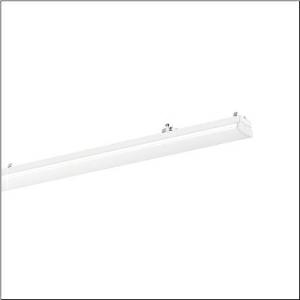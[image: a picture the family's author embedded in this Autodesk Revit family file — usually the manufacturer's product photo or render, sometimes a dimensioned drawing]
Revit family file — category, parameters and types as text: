
# Revit family: licross_21_recessed_opal_mo_52tl1ddv4e5g
name_source: partatom
category: Lighting Fixtures
units: mm (PartAtom-declared; Revit-internal decimal feet)

## family parameters
Cut with Voids When Loaded = No
Host = Face
Light Source = No
Part Type = Normal
Room Calculation Point = No
Round Connector Dimension = Use Diameter
Shared = No

## types (1)
- --- (1 x LED, 14620 lm, 85.3 W, 4000K)
    Apparent Load = 85 VA
    CIE Flux Codes = 44 73 91 87 100
    Color Rendering = 80
    Color Temperature = 4000K
    Default Elevation = 1800 mm
    Description = Licross 21 recessed opal MO, luminaire insert, of sheet steel, galvanised, coil coated, white, length: 2.250mm, width: 66mm, height: 67mm, LED rated luminous flux: 14.620lm, light colour: 840, SDCM (Standard Deviation of Colour Matching)MacAdam ≤ 3 SDCM (initial), control gear: DALI 2, with plug, 5-pole, with phase selection, mains connection: 220..240V, AC, 50/60Hz, rated input power: 85W, internal wiring halogen-free, primary optical cover: cover, of PMMA, light emission: direct with ceiling illumination distribution, primary light characteristic: symmetric, protection rating (complete): IP40, insulation class (complete): insulation class I (protective earthing), certification: CE, ENEC, VDE, UKCA, protection symbol: D if used in an environment without relevant dust loads with corresponding accessories, impact resistance: IK06, permissible ambient temperature for indoor applications: -25..+35°C, corresponds to IFS (International Featured Standards) requirements for safety and quality in the food industry, reducing of maximum allowable ambient temperature of 5°C with ceiling mounting, LABS conformity tested according to VDMA 24364:2018-05, The light source and the operating device comply with the requirements of the Ecodesign Regulation (EU) 2019/2020 and are replaceable in accordance with this regulation, packaging unit: 1 piece
    Height = 83 mm
    Lamp = 1 x LED
    Lamp Light Flux = 14620 lm
    Lamp Power = 85.3 W
    Lamp count = 1
    Length = 2250 mm
    Luminous efficacy = 171 lm/W
    Manufacturer = Siteco
    ModVariant = No
    Model = 52TL1DDV4E5G
    Mounting Place = Ceiling
    Mounting Type = Pendant
    Number of Poles = 1
    OnlyDefault = Yes
    Power Factor = 1
    Product Name = Licross 21 recessed opal MO
    Product group = luminaire insert | ceiling pendant
    ProductGroupID = 901
    Protection Class = Protection class I
    Protection Degree = IP 40
    RLX_Detail_Level = 1
    RLX_Emergency_Light_Flux = 0 lm
    RLX_Emergency_Type = 0
    RLX_Emergency_Type_DB = No
    RlxData = <blob elided: 27093 chars, md5=f61ae334>
    Socket = socket
    Standby Power = 0 W
    System Light Flux = 14620 lm
    System Power = 85 W
    Type Comments = factory setting: luminous flux: 100 % | dim-lin: 254 | 390 mA
    Type Image = l_1313666.jpg
    URL = http://relux.com
    VarID = @adj_072565
    Voltage = 0 V
    Weight = 0.00 kg
    Width = 76 mm

## geometry (parser evidence)
native form markers: Blend x4, Sweep x15
no freeform markers — native parametric forms only
